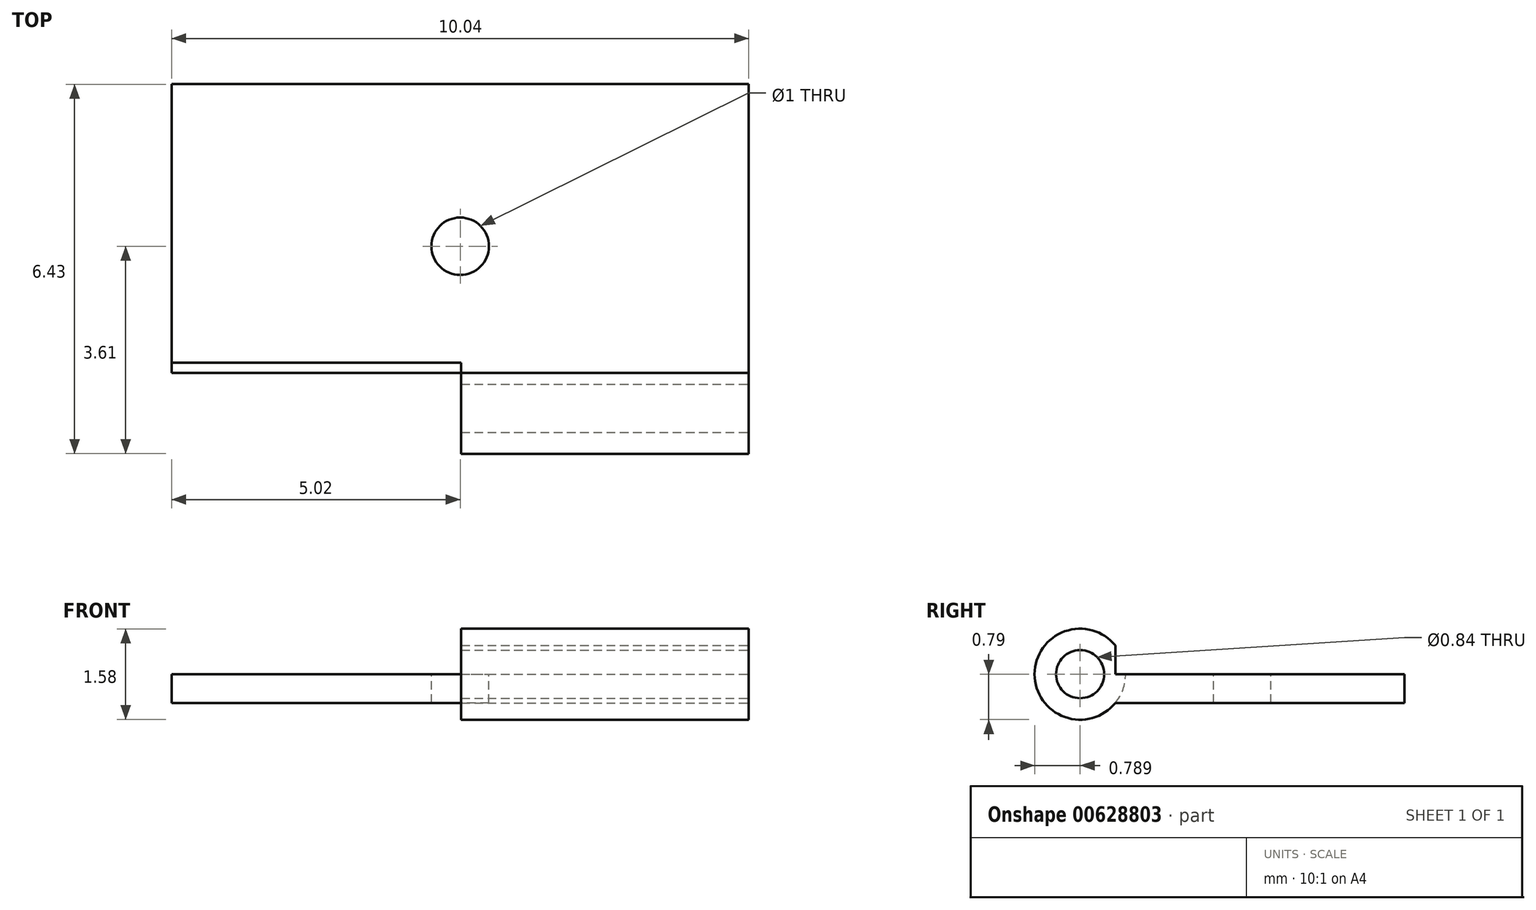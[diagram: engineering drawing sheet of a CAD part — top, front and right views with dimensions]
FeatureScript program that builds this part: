
annotation { "Feature Type Name" : "Feature", "Feature Type Description" : "" }
export const myFeature = defineFeature(function(context is Context, id is Id, definition is map)
    precondition{}
    {
        {
            var Q0;
            Q0=qCreatedBy(makeId("Top.planeOp"),FACE);
            var sketch = newSketch(context, id + "F0", { "sketchPlane" : qUnion([Q0])});
            skLineSegment(sketch, "E0.bottom", {"start": v(5.02, -2.82) * mm, "end": v(-5.02, -2.82) * mm});
            skLineSegment(sketch, "E0.top", {"start": v(5.02, 2.82) * mm, "end": v(-5.02, 2.82) * mm});
            skLineSegment(sketch, "E0.left", {"start": v(5.02, -2.82) * mm, "end": v(5.02, 2.82) * mm});
            skLineSegment(sketch, "E0.right", {"start": v(-5.02, -2.82) * mm, "end": v(-5.02, 2.82) * mm});
            skPoint(sketch, "E0.middle", {"position": v(0, 0) * mm});
            skSolve(sketch);
        }
        {
            var Q0;
            Q0=makeQuery(id+"F0.imprint","IMPRINT",FACE,{"disambiguationData":[TD([[makeQuery(id+"F0.imprint","IMPRINT",EDGE,{"derivedFrom":sQuery(id+"F0.wireOp",EDGE,"E0.bottom")}),-1.0]])]});
            extrude(context, id + "F1", {"entities" : qUnion([Q0]), "depth" : 1 * mm, "offsetDistance" : 25 * mm});
        }
        {
            var Q0;
            Q0=makeQuery(id+"F1.opExtrude","SWEPT_FACE",FACE,{"disambiguationData":[OSD([sQuery(id+"F0.wireOp",EDGE,"E0.left")])]});
            var sketch = newSketch(context, id + "F2", { "sketchPlane" : qUnion([Q0])});
            skCircle(sketch, "E1", {"center": v(-2.82, 0.5) * mm, "radius": 0.8 * mm});
            skSolve(sketch);
        }
        {
            var Q0;
            Q0 = qSketchRegion(id + "F2", true);
            extrude(context, id + "F3", {"entities" : qUnion([Q0]), "operationType" : NewBodyOperationType.REMOVE, "oppositeDirection" : true, "depth" : 10.55 * mm, "offsetDistance" : 25 * mm});
        }
        {
            var Q0;
            Q0 = qSketchRegion(id + "F2", true);
            extrude(context, id + "F4", {"entities" : qUnion([Q0]), "operationType" : NewBodyOperationType.ADD, "oppositeDirection" : true, "depth" : 5 * mm, "offsetDistance" : 25 * mm});
        }
        {
            var Q0;
            Q0=makeQuery(id+"F4.boolean.opBoolean","MERGE",FACE,{"derivedFrom":[makeQuery(id+"F1.opExtrude","SWEPT_FACE",FACE,{"disambiguationData":[OSD([sQuery(id+"F0.wireOp",EDGE,"E0.left")])]}),makeQuery(id+"F4.opExtrude","CAP_FACE",FACE,{"disambiguationData":[OSD([sQuery(id+"F2.wireOp",EDGE,"E1")])],"isStart":true})]});
            var sketch = newSketch(context, id + "F5", { "sketchPlane" : qUnion([Q0])});
            skCircle(sketch, "E2", {"center": v(-2.82, 0.5) * mm, "radius": 0.42 * mm});
            skSolve(sketch);
        }
        {
            var Q0;
            Q0 = qSketchRegion(id + "F5", true);
            extrude(context, id + "F6", {"entities" : qUnion([Q0]), "operationType" : NewBodyOperationType.REMOVE, "oppositeDirection" : true, "depth" : 25 * mm, "offsetDistance" : 25 * mm});
        }
        {
            var Q0;
            Q0=makeQuery(id+"F1.opExtrude","CAP_FACE",FACE,{"disambiguationData":[OSD([sQuery(id+"F0.wireOp",EDGE,"E0.bottom"),sQuery(id+"F0.wireOp",EDGE,"E0.top"),sQuery(id+"F0.wireOp",EDGE,"E0.left"),sQuery(id+"F0.wireOp",EDGE,"E0.right")])],"isStart":false});
            var sketch = newSketch(context, id + "F7", { "sketchPlane" : qUnion([Q0])});
            skPoint(sketch, "E3", {"position": v(0, 0) * mm});
            skSolve(sketch);
        }
        {
            var Q0;
            Q0=sQuery(id+"F7.wireOp",VERTEX,"E3");
            var Q1;
            Q1=makeQuery(id+"F1.opExtrude","SWEPT_BODY",BODY,{"disambiguationData":[OSD([sQuery(id+"F0.wireOp",EDGE,"E0.bottom"),sQuery(id+"F0.wireOp",EDGE,"E0.top"),sQuery(id+"F0.wireOp",EDGE,"E0.left"),sQuery(id+"F0.wireOp",EDGE,"E0.right")])]});
            hole(context, id + "F8", {"style" : HoleStyle.SIMPLE, "endStyle" : HoleEndStyle.BLIND, "holeDiameter" : 1 * mm, "majorDiameter" : 5 * mm, "holeDepth" : 2 * mm, "isTappedThrough" : true, "tappedDepth" : 12 * mm, "tapClearance" : 3, "locations" : qUnion([Q0]), "scope" : qUnion([Q1])});
        }
        {
            var Q0;
            Q0=makeQuery(id+"F4.boolean.opBoolean","MERGE",FACE,{"derivedFrom":[makeQuery(id+"F1.opExtrude","SWEPT_FACE",FACE,{"disambiguationData":[OSD([sQuery(id+"F0.wireOp",EDGE,"E0.left")])]}),makeQuery(id+"F4.opExtrude","CAP_FACE",FACE,{"disambiguationData":[OSD([sQuery(id+"F2.wireOp",EDGE,"E1")])],"isStart":true})]});
            var sketch = newSketch(context, id + "F9", { "sketchPlane" : qUnion([Q0])});
            skLineSegment(sketch, "E4.bottom", {"start": v(-2.2, 1) * mm, "end": v(2.82, 1) * mm});
            skLineSegment(sketch, "E4.top", {"start": v(-2.2, 0.5) * mm, "end": v(2.82, 0.5) * mm});
            skLineSegment(sketch, "E4.left", {"start": v(-2.2, 1) * mm, "end": v(-2.2, 0.5) * mm});
            skLineSegment(sketch, "E4.right", {"start": v(2.82, 1) * mm, "end": v(2.82, 0.5) * mm});
            skSolve(sketch);
        }
        {
            var Q0;
            Q0=makeQuery(id+"F9.imprint","IMPRINT",FACE,{"disambiguationData":[TD([[makeQuery(id+"F9.imprint","IMPRINT",EDGE,{"derivedFrom":sQuery(id+"F9.wireOp",EDGE,"E4.bottom")}),-1.0]])]});
            extrude(context, id + "F10", {"entities" : qUnion([Q0]), "operationType" : NewBodyOperationType.REMOVE, "oppositeDirection" : true, "depth" : 25 * mm, "offsetDistance" : 25 * mm});
        }
    });
